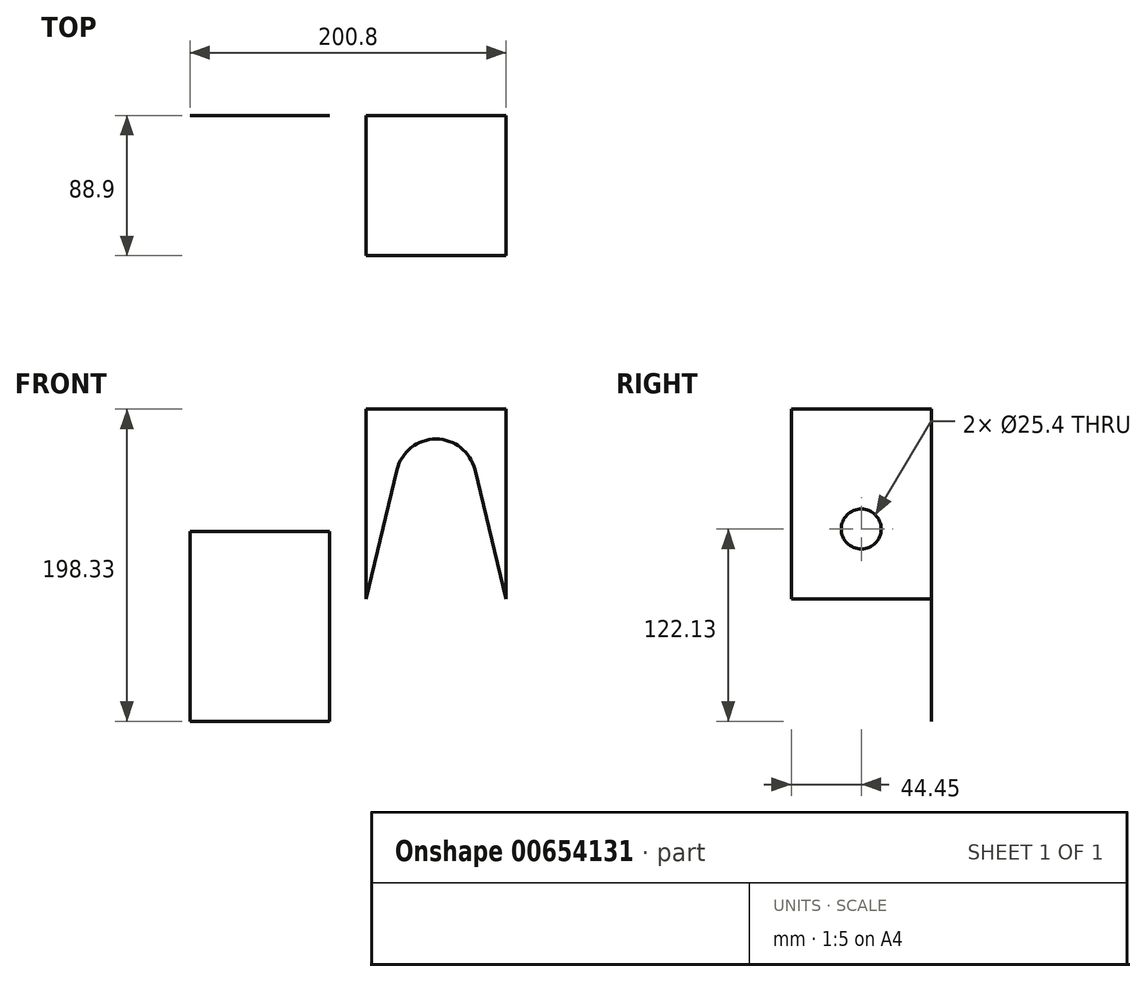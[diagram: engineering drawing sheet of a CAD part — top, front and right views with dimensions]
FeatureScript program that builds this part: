
annotation { "Feature Type Name" : "Feature", "Feature Type Description" : "" }
export const myFeature = defineFeature(function(context is Context, id is Id, definition is map)
    precondition{}
    {
        {
            var Q0;
            Q0=qCreatedBy(makeId("Front.planeOp"),FACE);
            var sketch = newSketch(context, id + "F0", { "sketchPlane" : qUnion([Q0])});
            skLineSegment(sketch, "E0.bottom", {"start": v(0, 0) * mm, "end": v(88.9, 0) * mm});
            skLineSegment(sketch, "E0.top", {"start": v(0, 120.65) * mm, "end": v(88.9, 120.65) * mm});
            skLineSegment(sketch, "E0.left", {"start": v(0, 0) * mm, "end": v(0, 120.65) * mm});
            skLineSegment(sketch, "E0.right", {"start": v(88.9, 0) * mm, "end": v(88.9, 120.65) * mm});
            skSolve(sketch);
        }
        {
            var Q0;
            Q0=qSketchRegion(id+"F0",true);
            extrude(context, id + "F1", {"entities" : qUnion([Q0]), "depth" : 88.9 * mm, "offsetDistance" : 25.4 * mm});
        }
        {
            var Q0;
            Q0=makeQuery(id+"F1.opExtrude","CAP_FACE",FACE,{"disambiguationData":[OSD([sQuery(id+"F0.wireOp",EDGE,"E0.bottom"),sQuery(id+"F0.wireOp",EDGE,"E0.top"),sQuery(id+"F0.wireOp",EDGE,"E0.left"),sQuery(id+"F0.wireOp",EDGE,"E0.right")])],"isStart":true});
            var sketch = newSketch(context, id + "F2", { "sketchPlane" : qUnion([Q0])});
            skLineSegment(sketch, "E1", {"start": v(0, 0) * mm, "end": v(-19.75, 82.14) * mm});
            skLineSegment(sketch, "E2", {"start": v(-88.9, 0) * mm, "end": v(-69.15, 82.14) * mm});
            skArc(sketch, "E3", {"start": v(-19.75, 82.14) * mm, "mid": v(-44.45, 101.6) * mm, "end": v(-69.15, 82.14) * mm});
            skLineSegment(sketch, "E4", {"start": v(-19.75, 82.14) * mm, "end": v(0, 82.14) * mm});
            skLineSegment(sketch, "E5", {"start": v(-69.15, 82.14) * mm, "end": v(-88.9, 82.14) * mm});
            skSolve(sketch);
        }
        {
            var Q0;
            Q0=makeQuery(id+"F1.opExtrude","SWEPT_FACE",FACE,{"disambiguationData":[OSD([sQuery(id+"F0.wireOp",EDGE,"E0.bottom")])]});
            shell(context, id + "F3", {"entities" : qUnion([Q0]), "thickness" : 0.03 * mm});
        }
        {
            var Q0;
            Q0=makeQuery(id+"F2.imprint","IMPRINT",FACE,{"disambiguationData":[TD([[makeQuery(id+"F2.imprint","IMPRINT",EDGE,{"derivedFrom":sQuery(id+"F2.wireOp",EDGE,"E1")}),1.0]])]});
            extrude(context, id + "F4", {"entities" : qUnion([Q0]), "operationType" : NewBodyOperationType.REMOVE, "oppositeDirection" : true, "depth" : 25.4 * mm, "offsetDistance" : 25.4 * mm});
        }
        {
            var Q0;
            Q0=makeQuery(id+"F1.opExtrude","SWEPT_FACE",FACE,{"disambiguationData":[OSD([sQuery(id+"F0.wireOp",EDGE,"E0.right")])]});
            var sketch = newSketch(context, id + "F5", { "sketchPlane" : qUnion([Q0])});
            skCircle(sketch, "E6", {"center": v(-44.45, 44.45) * mm, "radius": 12.7 * mm});
            skSolve(sketch);
        }
        {
            var Q0;
            Q0=makeQuery(id+"F5.imprint","IMPRINT",FACE,{"disambiguationData":[TD([[makeQuery(id+"F5.imprint","IMPRINT",EDGE,{"derivedFrom":sQuery(id+"F5.wireOp",EDGE,"E6")}),1.0]])]});
            extrude(context, id + "F6", {"entities" : qUnion([Q0]), "operationType" : NewBodyOperationType.REMOVE, "oppositeDirection" : true, "depth" : 127 * mm, "offsetDistance" : 25.4 * mm});
        }
        {
            var Q0;
            {var subQ0=sQuery(id+"F0.wireOp",EDGE,"E0.right");var subQ1=sQuery(id+"F0.wireOp",EDGE,"E0.left");var subQ2=sQuery(id+"F0.wireOp",EDGE,"E0.top");var subQ3=sQuery(id+"F0.wireOp",EDGE,"E0.bottom");Q0=makeQuery(id+"F3.opShell","OFFSET_FACE",FACE,{"disambiguationData":[OSD([subQ3,subQ2,subQ1,subQ0]),TDD([makeQuery(id+"F1.opExtrude","CAP_FACE",FACE,{"disambiguationData":[OSD([subQ3,subQ2,subQ1,subQ0])],"isStart":false})])]});}
            var sketch = newSketch(context, id + "F7", { "sketchPlane" : qUnion([Q0])});
            skSolve(sketch);
        }
        {
            var Q0;
            {var subQ0=sQuery(id+"F0.wireOp",EDGE,"E0.bottom");Q0=makeQuery(id+"F7.imprint","IMPRINT",FACE,{"disambiguationData":[TD([[makeQuery(id+"F7.imprint","IMPRINT",EDGE,{"derivedFrom":makeQuery(id+"F3.opShell","OFFSET_EDGE",EDGE,{"disambiguationData":[OSD([subQ0]),TDD([makeQuery(id+"F1.opExtrude","CAP_EDGE",EDGE,{"disambiguationData":[OSD([subQ0])],"isStart":false})])]})}),-1.0]])]});}
            extrude(context, id + "F8", {"entities" : qUnion([Q0]), "operationType" : NewBodyOperationType.REMOVE, "oppositeDirection" : true, "depth" : 12.7 * mm, "offsetDistance" : 25.4 * mm});
        }
        {
            var Q0;
            Q0=qCreatedBy(makeId("Front.planeOp"),FACE);
            var sketch = newSketch(context, id + "F9", { "sketchPlane" : qUnion([Q0])});
            skLineSegment(sketch, "E7", {"start": v(-111.9, 42.97) * mm, "end": v(-23, 42.97) * mm});
            skLineSegment(sketch, "E8", {"start": v(-23, 42.97) * mm, "end": v(-23, -77.68) * mm});
            skLineSegment(sketch, "E9", {"start": v(-23, -77.68) * mm, "end": v(-111.9, -77.68) * mm});
            skLineSegment(sketch, "E10", {"start": v(-111.9, -77.68) * mm, "end": v(-111.9, 42.97) * mm});
            skSolve(sketch);
        }
        {
            var Q0;
            Q0=makeQuery(id+"F9.imprint","IMPRINT",FACE,{"disambiguationData":[TD([[makeQuery(id+"F9.imprint","IMPRINT",EDGE,{"derivedFrom":sQuery(id+"F9.wireOp",EDGE,"E7")}),-1.0]])]});
            extrude(context, id + "F10", {"entities" : qUnion([Q0]), "depth" : 0.03 * mm, "offsetDistance" : 25.4 * mm});
        }
    });
